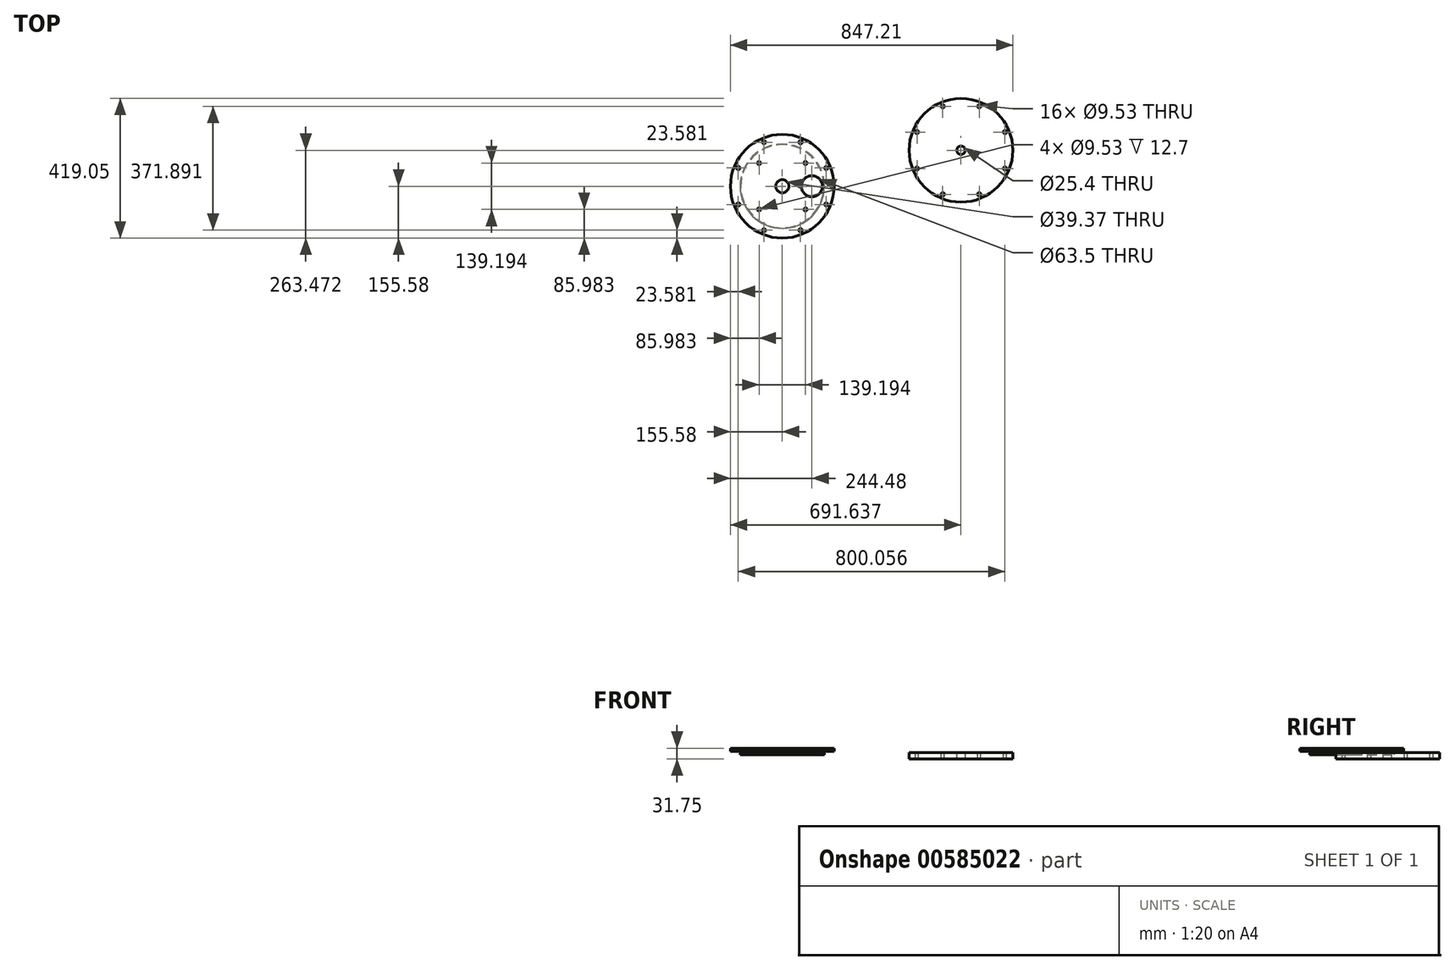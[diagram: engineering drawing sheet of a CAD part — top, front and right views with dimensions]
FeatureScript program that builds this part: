
annotation { "Feature Type Name" : "Feature", "Feature Type Description" : "" }
export const myFeature = defineFeature(function(context is Context, id is Id, definition is map)
    precondition{}
    {
        {
            var Q0;
            Q0=qCreatedBy(makeId("Top.planeOp"),FACE);
            var sketch = newSketch(context, id + "F0", { "sketchPlane" : qUnion([Q0])});
            skCircle(sketch, "E0", {"center": v(0, 0) * mm, "radius": 155.58 * mm});
            skCircle(sketch, "E1", {"center": v(0, 0) * mm, "radius": 19.69 * mm});
            skCircle(sketch, "E2", {"center": v(0, 0) * mm, "radius": 126.37 * mm});
            skSolve(sketch);
        }
        {
            var Q0;
            Q0 = qSketchRegion(id + "F0", true);
            var Q1;
            Q1=makeQuery(id+"F0.imprint","IMPRINT",FACE,{"disambiguationData":[TD([[makeQuery(id+"F0.imprint","IMPRINT",EDGE,{"derivedFrom":sQuery(id+"F0.wireOp",EDGE,"E2")}),1.0]])]});
            var Q2;
            Q2=makeQuery(id+"F0.imprint","IMPRINT",FACE,{"disambiguationData":[TD([[makeQuery(id+"F0.imprint","IMPRINT",EDGE,{"derivedFrom":sQuery(id+"F0.wireOp",EDGE,"E1")}),-1.0]])]});
            extrude(context, id + "F1", {"entities" : qUnion([Q0, Q1, Q2]), "depth" : 19.05 * mm, "offsetDistance" : 25.4 * mm});
        }
        {
            var Q0;
            Q0=makeQuery(id+"F0.imprint","IMPRINT",FACE,{"disambiguationData":[TD([[makeQuery(id+"F0.imprint","IMPRINT",EDGE,{"derivedFrom":sQuery(id+"F0.wireOp",EDGE,"E0")}),1.0]])]});
            extrude(context, id + "F2", {"entities" : qUnion([Q0]), "operationType" : NewBodyOperationType.REMOVE, "depth" : 9.52 * mm, "offsetDistance" : 25.4 * mm});
        }
        {
            var Q0;
            Q0=makeQuery(id+"F1.opExtrude","CAP_FACE",FACE,{"disambiguationData":[OSD([sQuery(id+"F0.wireOp",EDGE,"E0"),sQuery(id+"F0.wireOp",EDGE,"E1")])],"isStart":false});
            var sketch = newSketch(context, id + "F3", { "sketchPlane" : qUnion([Q0])});
            skCircle(sketch, "E3", {"center": v(0, 0) * mm, "radius": 142.88 * mm, "construction": true});
            skCircle(sketch, "E4", {"center": v(-54.68, 132) * mm, "radius": 4.76 * mm});
            skCircle(sketch, "E5.1.0", {"center": v(-132, 54.68) * mm, "radius": 4.76 * mm});
            skCircle(sketch, "E5.2.0", {"center": v(-132, -54.68) * mm, "radius": 4.76 * mm});
            skCircle(sketch, "E5.3.0", {"center": v(-54.68, -132) * mm, "radius": 4.76 * mm});
            skCircle(sketch, "E5.4.0", {"center": v(54.68, -132) * mm, "radius": 4.76 * mm});
            skCircle(sketch, "E5.5.0", {"center": v(132, -54.68) * mm, "radius": 4.76 * mm});
            skCircle(sketch, "E5.6.0", {"center": v(132, 54.68) * mm, "radius": 4.76 * mm});
            skCircle(sketch, "E5.7.0", {"center": v(54.68, 132) * mm, "radius": 4.76 * mm});
            skSolve(sketch);
        }
        {
            var Q0;
            Q0 = qSketchRegion(id + "F3", true);
            extrude(context, id + "F4", {"entities" : qUnion([Q0]), "operationType" : NewBodyOperationType.REMOVE, "oppositeDirection" : true, "depth" : 25.4 * mm, "offsetDistance" : 25.4 * mm});
        }
        {
            var Q0;
            {var subQ0=sQuery(id+"F0.wireOp",EDGE,"E1");Q0=makeQuery(id+"F2.boolean.opBoolean","SPLIT",FACE,{"disambiguationData":[TD([makeQuery(id+"F1.opExtrude","SWEPT_FACE",FACE,{"disambiguationData":[OSD([subQ0])]})])],"derivedFrom":makeQuery(id+"F1.opExtrude","CAP_FACE",FACE,{"disambiguationData":[OSD([sQuery(id+"F0.wireOp",EDGE,"E0"),subQ0])],"isStart":true})});}
            cPlane(context, id + "F5", {"entities" : qUnion([Q0]), "cplaneType" : CPlaneType.OFFSET, "offset" : 6.35 * mm, "oppositeDirection" : true, "width" : 152.4 * mm, "height" : 152.4 * mm});
        }
        {
            var Q0;
            Q0=qCreatedBy(id+"F5.planeOp",FACE);
            var sketch = newSketch(context, id + "F8", { "sketchPlane" : qUnion([Q0])});
            skCircle(sketch, "E6", {"center": v(536.06, -107.9) * mm, "radius": 155.58 * mm});
            skCircle(sketch, "E7", {"center": v(536.06, -107.9) * mm, "radius": 12.7 * mm});
            skSolve(sketch);
        }
        {
            var Q0;
            Q0 = qSketchRegion(id + "F8", true);
            extrude(context, id + "F9", {"entities" : qUnion([Q0]), "depth" : 19.05 * mm, "offsetDistance" : 25.4 * mm});
        }
        {
            var Q0;
            Q0=makeQuery(id+"F9.opExtrude","CAP_FACE",FACE,{"disambiguationData":[OSD([sQuery(id+"F8.wireOp",EDGE,"E6"),sQuery(id+"F8.wireOp",EDGE,"E7")])],"isStart":true});
            var sketch = newSketch(context, id + "F10", { "sketchPlane" : qUnion([Q0])});
            skCircle(sketch, "E8", {"center": v(536.06, 107.9) * mm, "radius": 142.88 * mm, "construction": true});
            skCircle(sketch, "E9", {"center": v(481.38, 239.9) * mm, "radius": 4.76 * mm});
            skCircle(sketch, "E10.1.0", {"center": v(404.06, 162.57) * mm, "radius": 4.76 * mm});
            skCircle(sketch, "E10.2.0", {"center": v(404.06, 53.22) * mm, "radius": 4.76 * mm});
            skCircle(sketch, "E10.3.0", {"center": v(481.38, -24.1) * mm, "radius": 4.76 * mm});
            skCircle(sketch, "E10.4.0", {"center": v(590.73, -24.1) * mm, "radius": 4.76 * mm});
            skCircle(sketch, "E10.5.0", {"center": v(668.06, 53.22) * mm, "radius": 4.76 * mm});
            skCircle(sketch, "E10.6.0", {"center": v(668.06, 162.57) * mm, "radius": 4.76 * mm});
            skCircle(sketch, "E10.7.0", {"center": v(590.73, 239.9) * mm, "radius": 4.76 * mm});
            skSolve(sketch);
        }
        {
            var Q0;
            Q0 = qSketchRegion(id + "F10", true);
            extrude(context, id + "F11", {"entities" : qUnion([Q0]), "operationType" : NewBodyOperationType.REMOVE, "oppositeDirection" : true, "depth" : 25.4 * mm, "offsetDistance" : 25.4 * mm});
        }
        {
            var Q0;
            {var subQ0=sQuery(id+"F0.wireOp",EDGE,"E0");Q0=makeQuery(id+"F7.boolean.opBoolean","SPLIT",FACE,{"disambiguationData":[TD([makeQuery(id+"F1.opExtrude","SWEPT_FACE",FACE,{"disambiguationData":[OSD([subQ0])]})])],"derivedFrom":makeQuery(id+"F1.opExtrude","CAP_FACE",FACE,{"disambiguationData":[OSD([subQ0,sQuery(id+"F0.wireOp",EDGE,"E1")])],"isStart":false})});}
            var sketch = newSketch(context, id + "F12", { "sketchPlane" : qUnion([Q0])});
            skCircle(sketch, "E11", {"center": v(88.9, 0) * mm, "radius": 31.75 * mm});
            skSolve(sketch);
        }
        {
            var Q0;
            Q0 = qSketchRegion(id + "F12", true);
            extrude(context, id + "F13", {"entities" : qUnion([Q0]), "operationType" : NewBodyOperationType.REMOVE, "oppositeDirection" : true, "depth" : 50.8 * mm, "offsetDistance" : 25.4 * mm});
        }
        {
            var Q0;
            {var subQ0=sQuery(id+"F0.wireOp",EDGE,"E0");Q0=makeQuery(id+"F7.boolean.opBoolean","SPLIT",FACE,{"disambiguationData":[TD([makeQuery(id+"F1.opExtrude","SWEPT_FACE",FACE,{"disambiguationData":[OSD([subQ0])]})])],"derivedFrom":makeQuery(id+"F1.opExtrude","CAP_FACE",FACE,{"disambiguationData":[OSD([subQ0,sQuery(id+"F0.wireOp",EDGE,"E1")])],"isStart":false})});}
            var sketch = newSketch(context, id + "F14", { "sketchPlane" : qUnion([Q0])});
            skCircle(sketch, "E12", {"center": v(-69.6, 69.6) * mm, "radius": 4.76 * mm});
            skCircle(sketch, "E13", {"center": v(0, 0) * mm, "radius": 98.43 * mm, "construction": true});
            skCircle(sketch, "E14.1.0", {"center": v(-69.6, -69.6) * mm, "radius": 4.76 * mm});
            skCircle(sketch, "E14.2.0", {"center": v(69.6, -69.6) * mm, "radius": 4.76 * mm});
            skCircle(sketch, "E14.3.0", {"center": v(69.6, 69.6) * mm, "radius": 4.76 * mm});
            skSolve(sketch);
        }
        {
            var Q0;
            Q0 = qSketchRegion(id + "F14", true);
            extrude(context, id + "F15", {"entities" : qUnion([Q0]), "operationType" : NewBodyOperationType.REMOVE, "oppositeDirection" : true, "depth" : 12.7 * mm, "offsetDistance" : 25.4 * mm});
        }
        {
            var Q0;
            Q0=makeQuery(id+"F1.opExtrude","CAP_FACE",FACE,{"disambiguationData":[OSD([sQuery(id+"F0.wireOp",EDGE,"E0"),sQuery(id+"F0.wireOp",EDGE,"E1")])],"isStart":true});
            cPlane(context, id + "F16", {"entities" : qUnion([Q0]), "cplaneType" : CPlaneType.OFFSET, "offset" : 3.17 * mm, "oppositeDirection" : true, "width" : 152.4 * mm, "height" : 152.4 * mm});
        }
        {
            var Q0;
            Q0=qCreatedBy(id+"F16.planeOp",FACE);
            var sketch = newSketch(context, id + "F17", { "sketchPlane" : qUnion([Q0])});
            skCircle(sketch, "E15", {"center": v(0, 0) * mm, "radius": 124.78 * mm});
            skCircle(sketch, "E16", {"center": v(0, 0) * mm, "radius": 127 * mm});
            skSolve(sketch);
        }
        {
            var Q0;
            Q0 = qSketchRegion(id + "F17", true);
            extrude(context, id + "F18", {"entities" : qUnion([Q0]), "operationType" : NewBodyOperationType.REMOVE, "oppositeDirection" : true, "depth" : 3.17 * mm, "offsetDistance" : 25.4 * mm});
        }
        {
            var Q0;
            Q0=makeQuery(id+"F18.boolean.opBoolean","INTERSECT",EDGE,{"derivedFrom":[makeQuery(id+"F2.boolean.opBoolean","COPY",FACE,{"derivedFrom":makeQuery(id+"F2.opExtrude","SWEPT_FACE",FACE,{"disambiguationData":[OSD([sQuery(id+"F0.wireOp",EDGE,"E2")])]})}),makeQuery(id+"F18.opExtrude","CAP_FACE",FACE,{"disambiguationData":[OSD([sQuery(id+"F17.wireOp",EDGE,"E15"),sQuery(id+"F17.wireOp",EDGE,"E16")])],"isStart":false})]});
            var Q1;
            Q1=makeQuery(id+"F18.boolean.opBoolean","INTERSECT",EDGE,{"derivedFrom":[makeQuery(id+"F2.boolean.opBoolean","COPY",FACE,{"derivedFrom":makeQuery(id+"F2.opExtrude","SWEPT_FACE",FACE,{"disambiguationData":[OSD([sQuery(id+"F0.wireOp",EDGE,"E2")])]})}),makeQuery(id+"F18.opExtrude","CAP_FACE",FACE,{"disambiguationData":[OSD([sQuery(id+"F17.wireOp",EDGE,"E15"),sQuery(id+"F17.wireOp",EDGE,"E16")])],"isStart":true})]});
            chamfer(context, id + "F19", {"entities" : qUnion([Q0, Q1]), "width" : 0.25 * mm, "tangentPropagation" : true});
        }
    });
